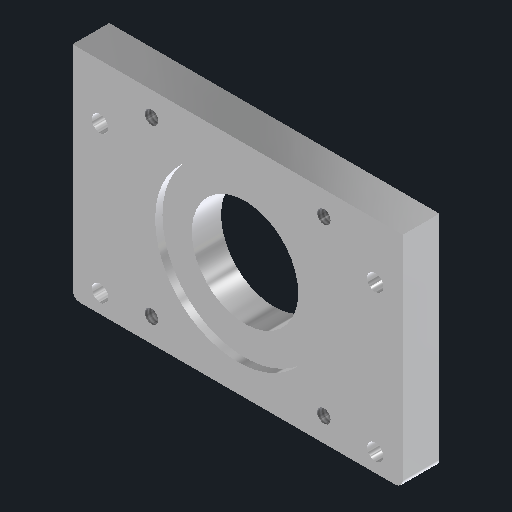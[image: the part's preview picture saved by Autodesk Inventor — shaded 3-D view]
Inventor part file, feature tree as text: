
AUTODESK INVENTOR PART (.ipt)
format: ipt  version: 2022 (Build 260153000, 153)  size: 157,184 bytes
history: native  units: mm
features: reference x6, other x5, sketch x4, extrude x2, hole x2, projected_geometry x1
ambient origin geometry x8: Origin, YZ Plane, XZ Plane, XY Plane, X Axis, Y Axis, Z Axis, Center Point
bodies: Solid1 (feature_tree)
feature tree (20):
  extrude  "Extrusion1"  Depth=8.0mm TaperAngle=0.0deg
  extrude  "Extrusion2"  Depth=30.0mm
  hole  "Hole2"  [1 undecoded]
  hole  "Hole3"  [1 undecoded]
  sketch  "Sketch1"  dims[d1=2.0mm d2=8.0mm d3=0.0mm]
  reference  "Reference1"
  reference  "Reference2"
  sketch  "Sketch5"  dims[d6=30.0mm d7=30.0mm]
  reference  "Reference7"
  reference  "Reference8"
  reference  "Reference9"
  reference  "Reference10"
  sketch  "Sketch6"  dims[d18=3.683mm d19=5.0mm d20=8.0mm d21=4.6mm d22=90.0deg d23=6.0mm d24=20.594885mm d25=45.0mm]
  projected_geometry  "Projected Loop1"
  sketch  "Sketch7"  dims[d26=2.0mm d27=0.0mm d28=75.0mm d29=40.0mm d30=5.0mm d31=4.5mm d32=6.0mm d33=8.0mm d34=4.6mm d35=90.0deg d36=8.0mm d37=20.594885mm]
  other  "Assembly2.iam"
  other  "Soporte:1"
  other  "Bevel Gears:1"
  other  "Bevel Gear2:1"
  other  "NEMA 23 - 76mm:1"
note: 2 required parameter values undecoded (feature->parameter linkage not recoverable at this tier; creation-order binding heuristic only, values carry confidence <= 0.55)
